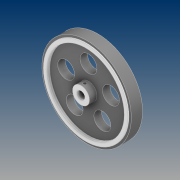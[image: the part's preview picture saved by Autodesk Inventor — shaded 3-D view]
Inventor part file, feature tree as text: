
AUTODESK INVENTOR PART (.ipt)
format: ipt  version: 2021 (Build 250183000, 183)  size: 207,360 bytes
history: imported  units: mm
features: sketch x1, other x1, imported_body x1
ambient origin geometry x8: Origin, YZ Plane, XZ Plane, XY Plane, X Axis, Y Axis, Z Axis, Center Point
bodies: Solid1 (imported_parasolid)
feature tree (3):
  sketch  "Sketch1"
  other  "Cut-Extrude6"
  imported_body  NMx_Import_Brep_tag  [imported B-rep: ~15 faces, bbox_mm=[92.5, 0.0, 14.0]]
